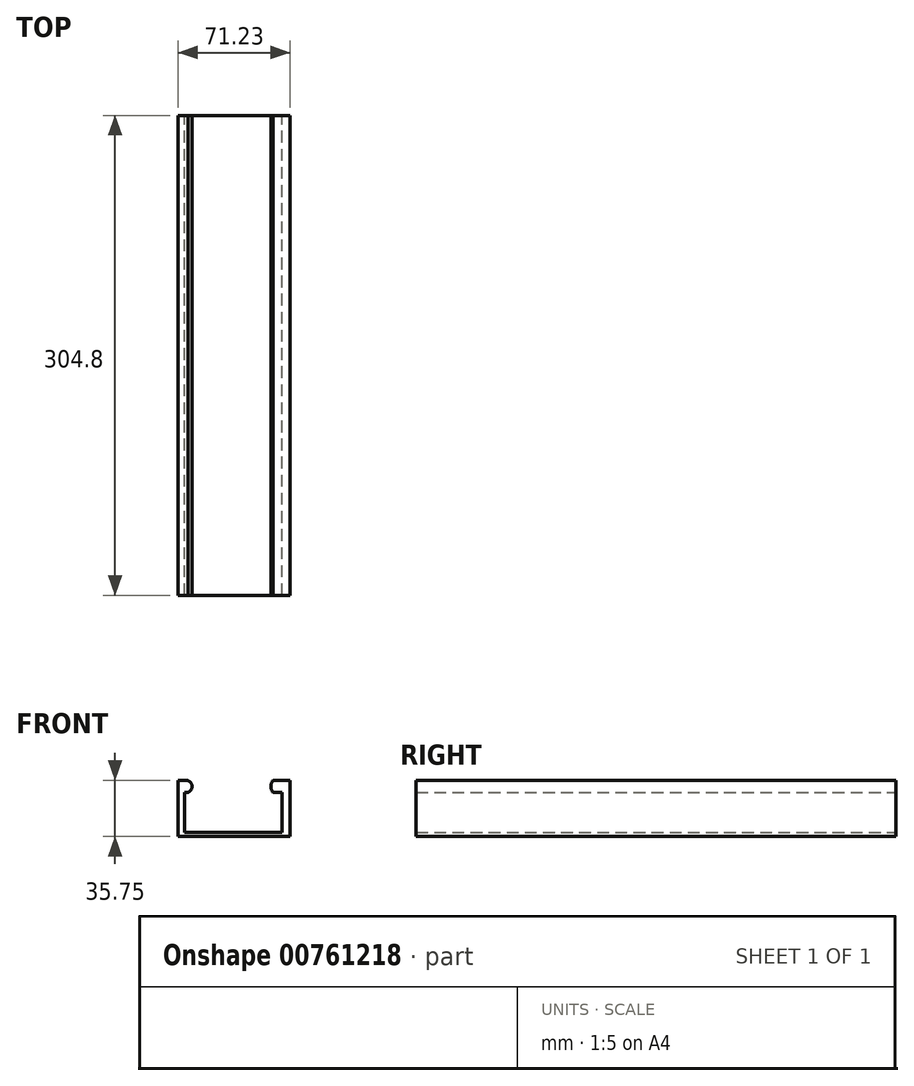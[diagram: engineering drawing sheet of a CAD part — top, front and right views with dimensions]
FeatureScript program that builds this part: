
annotation { "Feature Type Name" : "Feature", "Feature Type Description" : "" }
export const myFeature = defineFeature(function(context is Context, id is Id, definition is map)
    precondition{}
    {
        {
            var Q0;
            Q0=qCreatedBy(makeId("Front.planeOp"),FACE);
            var sketch = newSketch(context, id + "F0", { "sketchPlane" : qUnion([Q0])});
            skLineSegment(sketch, "E0", {"start": v(22.98, 19.54) * mm, "end": v(22.98, -16.2) * mm});
            skLineSegment(sketch, "E1", {"start": v(22.98, -16.2) * mm, "end": v(-48.25, -16.2) * mm});
            skLineSegment(sketch, "E2", {"start": v(-48.25, -16.2) * mm, "end": v(-48.25, 19.35) * mm});
            skLineSegment(sketch, "E3", {"start": v(-42.05, 11.73) * mm, "end": v(-44.22, 11.73) * mm});
            skLineSegment(sketch, "E4", {"start": v(-44.22, 11.73) * mm, "end": v(-44.22, -13.67) * mm});
            skLineSegment(sketch, "E5", {"start": v(-44.22, -13.67) * mm, "end": v(17.78, -13.67) * mm});
            skLineSegment(sketch, "E6", {"start": v(17.78, -13.67) * mm, "end": v(17.78, 11.73) * mm});
            skLineSegment(sketch, "E7", {"start": v(17.78, 11.73) * mm, "end": v(11.94, 11.73) * mm});
            skLineSegment(sketch, "E8", {"start": v(11.95, 19.38) * mm, "end": v(22.98, 19.54) * mm});
            skLineSegment(sketch, "E9", {"start": v(-42.06, 19.36) * mm, "end": v(-48.25, 19.35) * mm});
            skPoint(sketch, "E10.centerSnap0", {"position": v(10.28, 15.54) * mm});
            skArc(sketch, "E11", {"start": v(-42.05, 11.73) * mm, "mid": v(-39.42, 15.55) * mm, "end": v(-42.06, 19.36) * mm});
            skArc(sketch, "E12.trimOffspring", {"start": v(11.95, 19.38) * mm, "mid": v(10.65, 15.56) * mm, "end": v(11.94, 11.73) * mm});
            skSolve(sketch);
        }
        {
            var Q0;
            Q0 = qSketchRegion(id + "F0", true);
            extrude(context, id + "F1", {"entities" : qUnion([Q0]), "depth" : 304.8 * mm, "offsetDistance" : 25.4 * mm});
        }
    });
